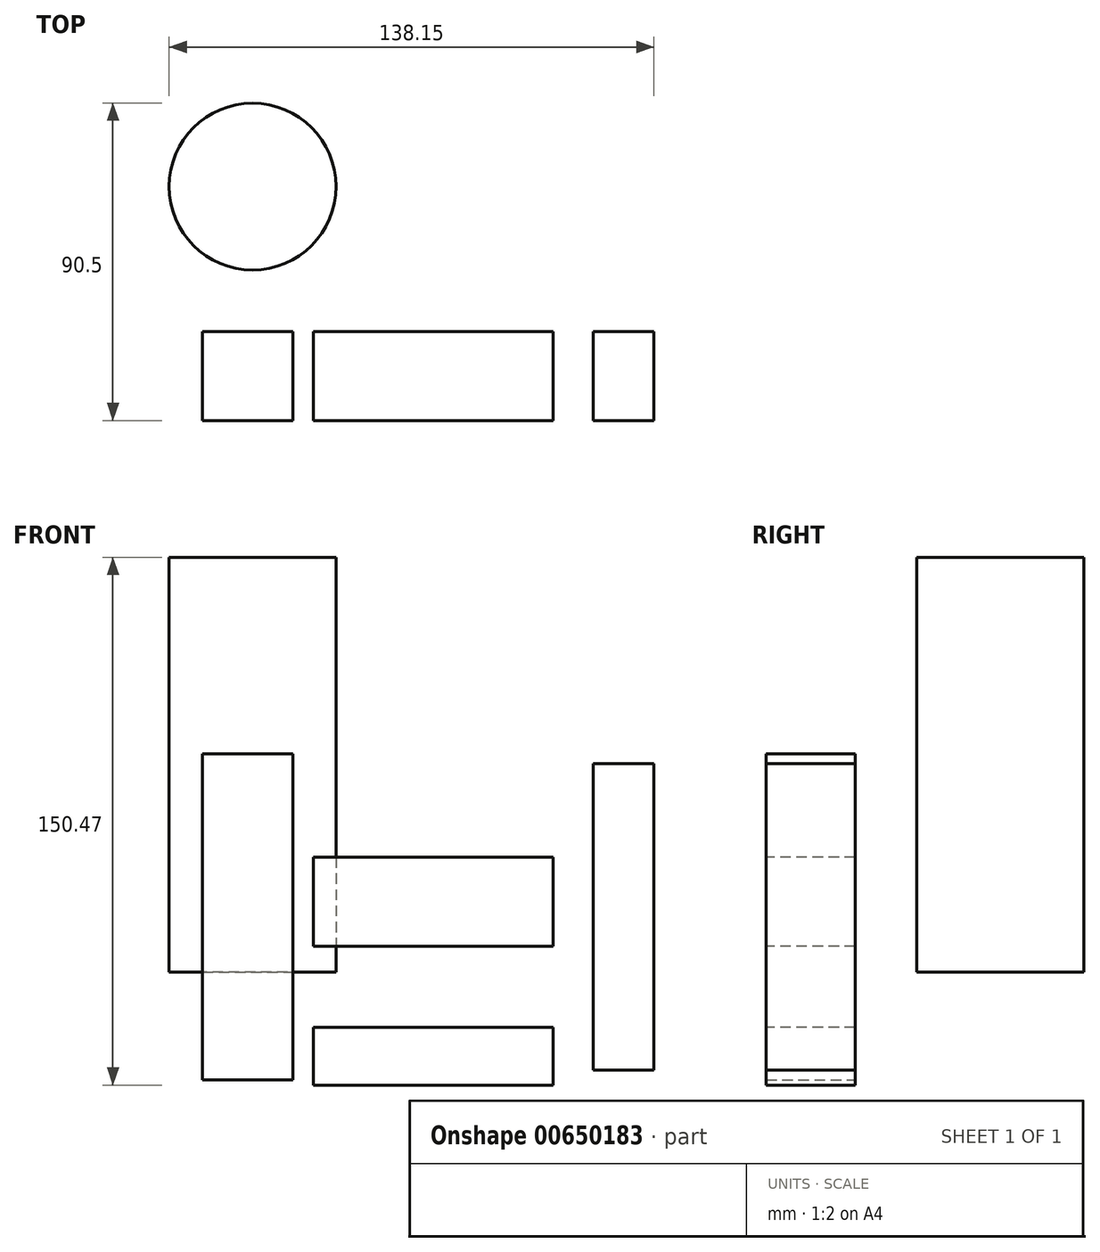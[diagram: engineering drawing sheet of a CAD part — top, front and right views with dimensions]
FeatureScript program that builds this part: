
annotation { "Feature Type Name" : "Feature", "Feature Type Description" : "" }
export const myFeature = defineFeature(function(context is Context, id is Id, definition is map)
    precondition{}
    {
        {
            var Q0;
            Q0=qCreatedBy(makeId("Front.planeOp"),FACE);
            var sketch = newSketch(context, id + "F0", { "sketchPlane" : qUnion([Q0])});
            skLineSegment(sketch, "E0.bottom", {"start": v(-35.41, 32.73) * mm, "end": v(32.83, 32.73) * mm});
            skLineSegment(sketch, "E0.top", {"start": v(-35.41, -32.24) * mm, "end": v(32.83, -32.24) * mm});
            skLineSegment(sketch, "E0.left", {"start": v(-35.41, 32.73) * mm, "end": v(-35.41, -32.24) * mm});
            skLineSegment(sketch, "E0.right", {"start": v(32.83, 32.73) * mm, "end": v(32.83, -32.24) * mm});
            skSolve(sketch);
        }
        {
            var Q0;
            Q0=qCreatedBy(makeId("Front.planeOp"),FACE);
            var sketch = newSketch(context, id + "F1", { "sketchPlane" : qUnion([Q0])});
            skLineSegment(sketch, "E1.bottom", {"start": v(-67.04, 62.23) * mm, "end": v(-41.34, 62.23) * mm});
            skLineSegment(sketch, "E1.top", {"start": v(-67.04, -30.8) * mm, "end": v(-41.34, -30.8) * mm});
            skLineSegment(sketch, "E1.left", {"start": v(-67.04, 62.23) * mm, "end": v(-67.04, -30.8) * mm});
            skLineSegment(sketch, "E1.right", {"start": v(-41.34, 62.23) * mm, "end": v(-41.34, -30.8) * mm});
            skLineSegment(sketch, "E2.bottom", {"start": v(44.24, -28.03) * mm, "end": v(61.56, -28.03) * mm});
            skLineSegment(sketch, "E2.top", {"start": v(44.24, 59.38) * mm, "end": v(61.56, 59.38) * mm});
            skLineSegment(sketch, "E2.left", {"start": v(44.24, -28.03) * mm, "end": v(44.24, 59.38) * mm});
            skLineSegment(sketch, "E2.right", {"start": v(61.56, -28.03) * mm, "end": v(61.56, 59.38) * mm});
            skSolve(sketch);
        }
        {
            var Q0;
            Q0=makeQuery(id+"F1.imprint","IMPRINT",FACE,{"disambiguationData":[TD([[makeQuery(id+"F1.imprint","IMPRINT",EDGE,{"derivedFrom":sQuery(id+"F1.wireOp",EDGE,"E1.bottom")}),-1.0]])]});
            extrude(context, id + "F2", {"entities" : qUnion([Q0]), "depth" : 25.4 * mm, "offsetDistance" : 25.4 * mm});
        }
        {
            var Q0;
            Q0=sQuery(id+"F0.wireOp",EDGE,"E0.bottom");
            var Q1;
            Q1=sQuery(id+"F0.wireOp",EDGE,"E0.right");
            var Q2;
            Q2=sQuery(id+"F0.wireOp",EDGE,"E0.top");
            var Q3;
            Q3=sQuery(id+"F0.wireOp",EDGE,"E0.left");
            extrude(context, id + "F3", {"bodyType" : ToolBodyType.SURFACE, "surfaceEntities" : qUnion([Q0, Q1, Q2, Q3]), "depth" : 25.4 * mm, "offsetDistance" : 25.4 * mm});
        }
        {
            var Q0;
            Q0 = qSketchRegion(id + "F1", true);
            extrude(context, id + "F4", {"entities" : qUnion([Q0]), "operationType" : NewBodyOperationType.ADD, "depth" : 25.4 * mm, "offsetDistance" : 25.4 * mm});
        }
        {
            var Q0;
            Q0=makeQuery(id+"F3.opExtrude","SWEPT_FACE",FACE,{"disambiguationData":[OSD([sQuery(id+"F0.wireOp",EDGE,"E0.bottom")])]});
            extrude(context, id + "F5", {"entities" : qUnion([Q0]), "depth" : 25.4 * mm, "offsetDistance" : 25.4 * mm});
        }
        {
            var Q0;
            Q0=makeQuery(id+"F3.opExtrude","SWEPT_FACE",FACE,{"disambiguationData":[OSD([sQuery(id+"F0.wireOp",EDGE,"E0.top")])]});
            extrude(context, id + "F6", {"entities" : qUnion([Q0]), "depth" : 16.46 * mm, "offsetDistance" : 25.4 * mm});
        }
        {
            var Q0;
            Q0=qCreatedBy(makeId("Top.planeOp"),FACE);
            var sketch = newSketch(context, id + "F7", { "sketchPlane" : qUnion([Q0])});
            skCircle(sketch, "E3", {"center": v(-52.81, 41.32) * mm, "radius": 23.78 * mm});
            skSolve(sketch);
        }
        {
            var Q0;
            Q0 = qSketchRegion(id + "F7", true);
            extrude(context, id + "F8", {"entities" : qUnion([Q0]), "depth" : 118.23 * mm, "offsetDistance" : 25.4 * mm});
        }
    });
